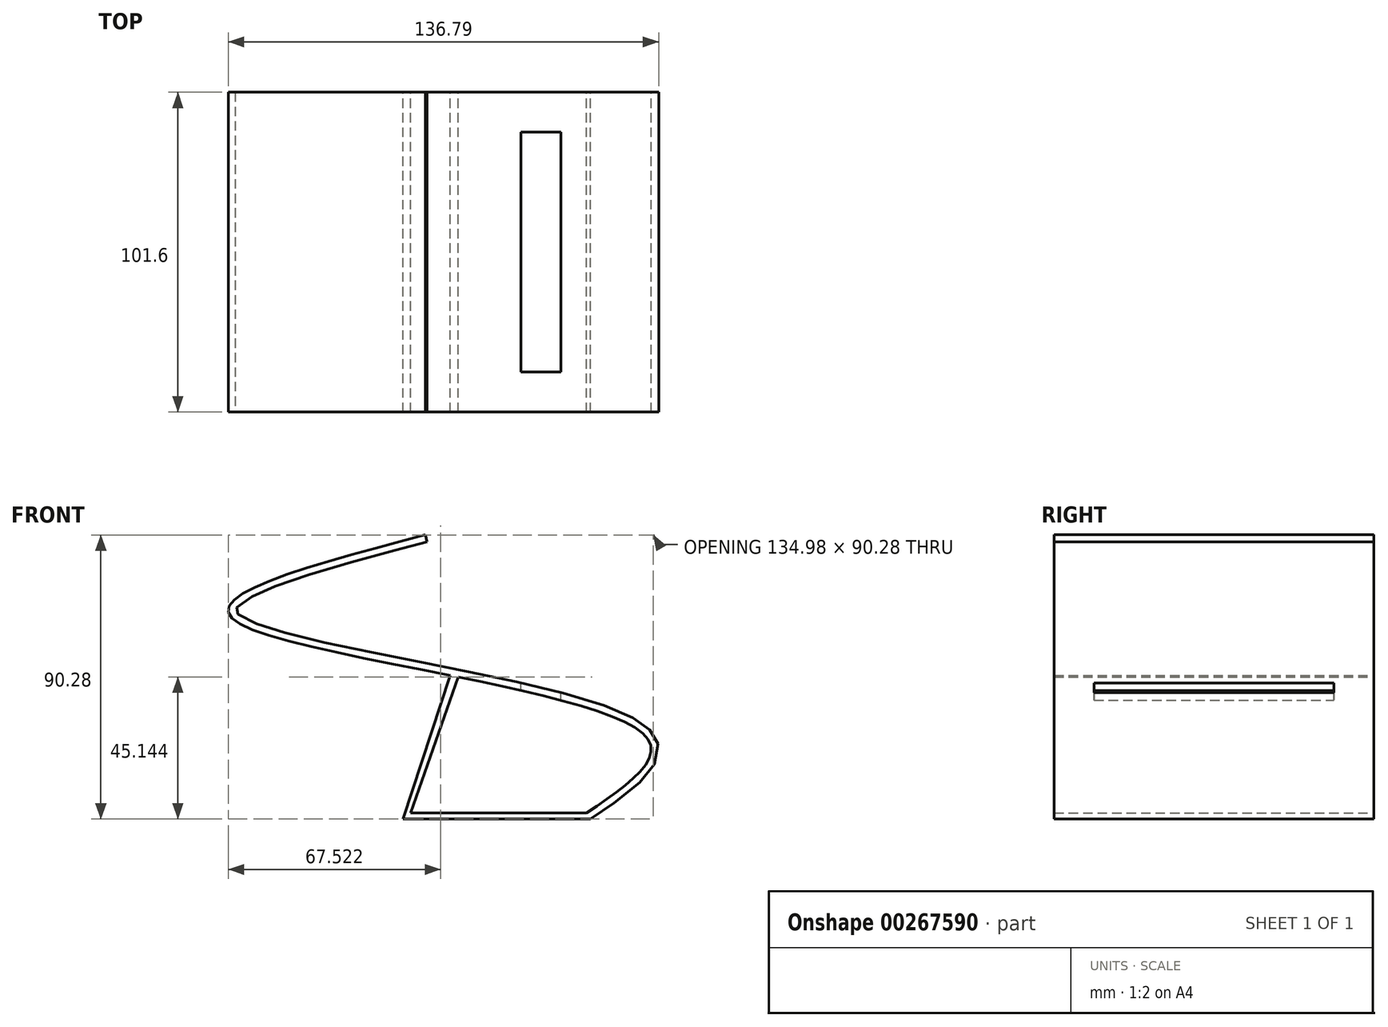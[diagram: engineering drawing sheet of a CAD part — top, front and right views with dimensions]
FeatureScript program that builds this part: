
annotation { "Feature Type Name" : "Feature", "Feature Type Description" : "" }
export const myFeature = defineFeature(function(context is Context, id is Id, definition is map)
    precondition{}
    {
        {
            var Q0;
            Q0=qCreatedBy(makeId("Front.planeOp"),FACE);
            var sketch = newSketch(context, id + "F0", { "sketchPlane" : qUnion([Q0])});
            skFitSpline(sketch, "E0", {"points": [v(-30.35, 46.74) * mm, v(-91.55, 20.03) * mm, v(39.34, -16.88) * mm, v(20.89, -41.64) * mm], "startDerivative": vector(-327.47, -86.14) * mm, "endDerivative": vector(-175.54, -119.17) * mm});
            skFitSpline(sketch, "E1.0", {"points": [v(-29.77, 44.53) * mm, v(-33.18, 43.64) * mm, v(-40, 41.84) * mm, v(-49.97, 39.16) * mm, v(-59.44, 36.5) * mm, v(-68.17, 33.85) * mm, v(-74.6, 31.68) * mm, v(-79.12, 29.96) * mm, v(-82.15, 28.7) * mm, v(-84.8, 27.45) * mm, v(-87.01, 26.24) * mm, v(-88.75, 25.1) * mm, v(-89.76, 24.22) * mm, v(-90.28, 23.63) * mm, v(-90.54, 23.26) * mm, v(-90.66, 22.98) * mm, v(-90.7, 22.81) * mm, v(-90.7, 22.72) * mm, v(-90.7, 22.62) * mm, v(-90.63, 22.46) * mm, v(-90.46, 22.18) * mm, v(-90.12, 21.82) * mm, v(-89.44, 21.23) * mm, v(-88.11, 20.38) * mm, v(-85.86, 19.3) * mm, v(-83.02, 18.18) * mm, v(-79.66, 17.05) * mm, v(-74.57, 15.54) * mm, v(-67.17, 13.65) * mm, v(-57, 11.38) * mm, v(-45.9, 9.08) * mm, v(-34.18, 6.76) * mm, v(-22.21, 4.39) * mm, v(-10.31, 1.96) * mm, v(1.18, -0.55) * mm, v(11.93, -3.15) * mm, v(21.61, -5.86) * mm, v(28.54, -8.24) * mm, v(33.25, -10.24) * mm, v(36.34, -11.8) * mm, v(38.52, -13.18) * mm, v(40.02, -14.36) * mm, v(41.03, -15.3) * mm, v(41.89, -16.28) * mm, v(42.6, -17.33) * mm, v(43.14, -18.44) * mm, v(43.63, -19.98) * mm, v(43.78, -21.96) * mm, v(43.3, -24.24) * mm, v(42.34, -26.37) * mm, v(40.98, -28.39) * mm, v(39.31, -30.34) * mm, v(36.72, -32.9) * mm, v(32.9, -36.04) * mm, v(27.68, -39.8) * mm, v(24, -42.3) * mm, v(22.17, -43.54) * mm]});
            skLineSegment(sketch, "E2", {"start": v(-29.77, 44.53) * mm, "end": v(-30.35, 46.74) * mm});
            skLineSegment(sketch, "E3", {"start": v(22.17, -43.54) * mm, "end": v(-37.4, -43.54) * mm});
            skLineSegment(sketch, "E4", {"start": v(20.89, -41.64) * mm, "end": v(-34.96, -41.64) * mm});
            skLineSegment(sketch, "E5", {"start": v(-37.4, -43.54) * mm, "end": v(-22.47, 2.1) * mm});
            skLineSegment(sketch, "E6", {"start": v(-34.96, -41.64) * mm, "end": v(-19.96, 1.59) * mm});
            skSolve(sketch);
        }
        {
            var Q0;
            Q0 = qSketchRegion(id + "F0", true);
            extrude(context, id + "F1", {"entities" : qUnion([Q0]), "depth" : 101.6 * mm});
        }
        {
            var Q0;
            Q0=qCreatedBy(makeId("Top.planeOp"),FACE);
            var sketch = newSketch(context, id + "F2", { "sketchPlane" : qUnion([Q0])});
            skLineSegment(sketch, "E7.bottom", {"start": v(0, -12.7) * mm, "end": v(12.7, -12.7) * mm});
            skLineSegment(sketch, "E7.top", {"start": v(0, -88.9) * mm, "end": v(12.7, -88.9) * mm});
            skLineSegment(sketch, "E7.left", {"start": v(0, -12.7) * mm, "end": v(0, -88.9) * mm});
            skLineSegment(sketch, "E7.right", {"start": v(12.7, -12.7) * mm, "end": v(12.7, -88.9) * mm});
            skSolve(sketch);
        }
        {
            var Q0;
            Q0 = qSketchRegion(id + "F2", true);
            extrude(context, id + "F3", {"entities" : qUnion([Q0]), "operationType" : NewBodyOperationType.REMOVE, "oppositeDirection" : true, "depth" : 25.4 * mm});
        }
    });
